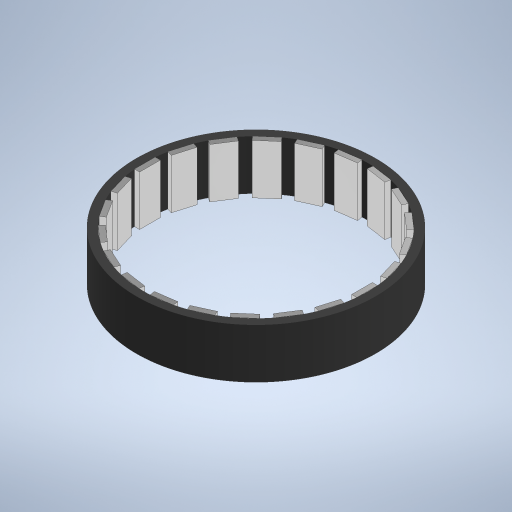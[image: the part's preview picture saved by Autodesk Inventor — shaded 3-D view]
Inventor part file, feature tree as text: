
AUTODESK INVENTOR PART (.ipt)
format: ipt  version: 2023.1 (Build 271208000, 208)  size: 456,192 bytes
history: native  units: in
note: dims shown in document units (in); Inventor stores cm internally (conversion verified against a paired STEP export)
features: extrude x2, sketch x2
ambient origin geometry x8: Origin, YZ Plane, XZ Plane, XY Plane, X Axis, Y Axis, Z Axis, Center Point
bodies: Solid1 (feature_tree)
feature tree (4):
  extrude  "Extrusion1"  Depth=0.0591in
  extrude  "Extrusion2"  Depth=0.0394in
  sketch  "Sketch1"  dims[d0=1.815in d1=0.0591in]
  sketch  "Sketch2"  dims[d2=0.378in d3=0.0in d4=0.0394in d5=0.1575in d6=8.6614in d8=360.0deg d10=0.378in d11=0.0in]
